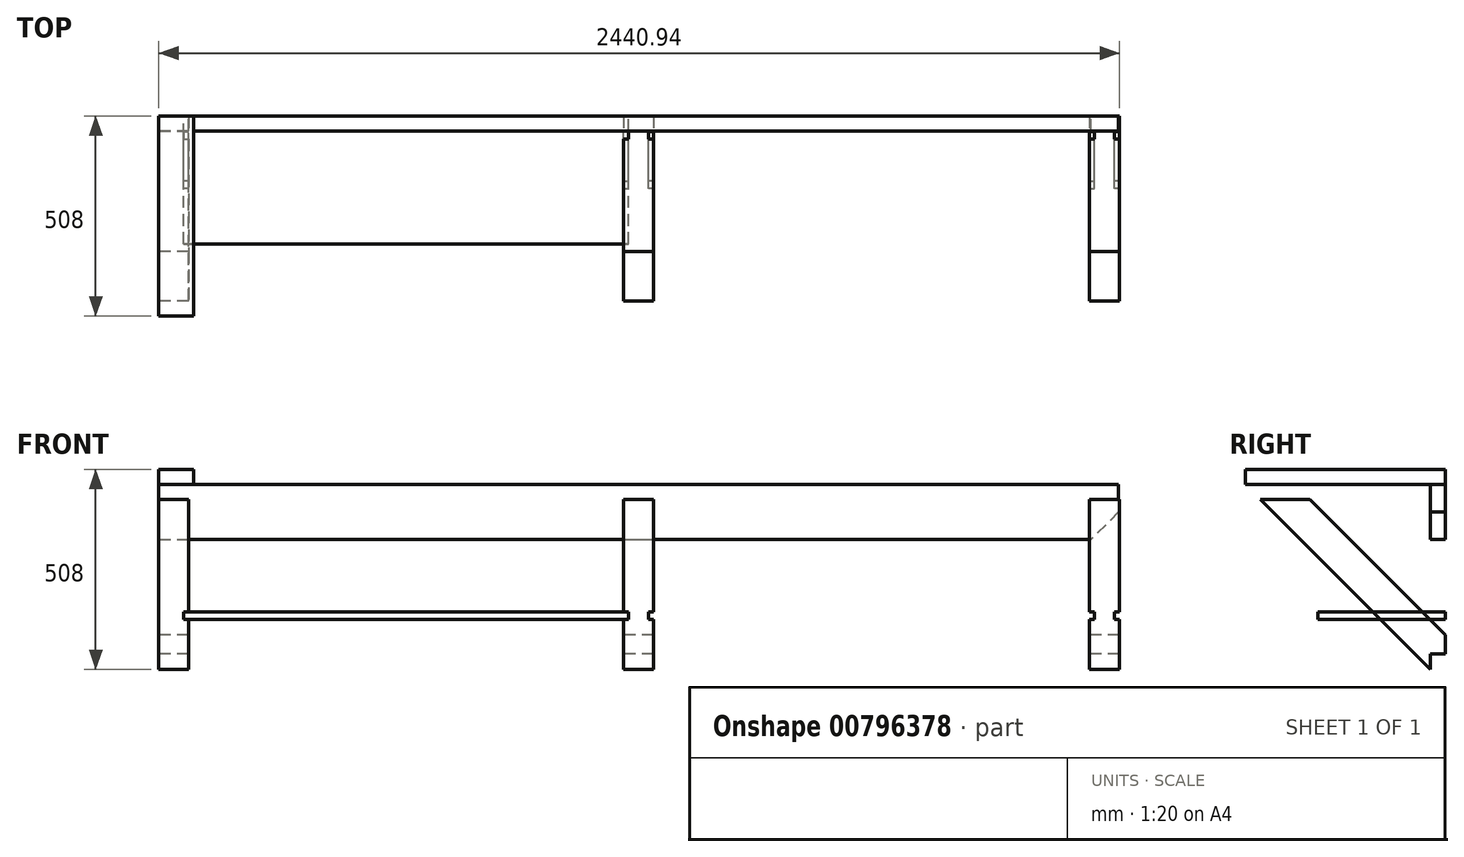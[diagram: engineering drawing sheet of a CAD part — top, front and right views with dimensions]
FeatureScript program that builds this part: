
annotation { "Feature Type Name" : "Feature", "Feature Type Description" : "" }
export const myFeature = defineFeature(function(context is Context, id is Id, definition is map)
    precondition{}
    {
        {
            var Q0;
            Q0=qCreatedBy(makeId("Front.planeOp"),FACE);
            var sketch = newSketch(context, id + "F0", { "sketchPlane" : qUnion([Q0])});
            skLineSegment(sketch, "E0.bottom", {"start": v(0, 0) * mm, "end": v(2438.4, 0) * mm});
            skLineSegment(sketch, "E0.top", {"start": v(0, -139.7) * mm, "end": v(2368.55, -139.7) * mm});
            skLineSegment(sketch, "E0.left", {"start": v(0, 0) * mm, "end": v(0, -139.7) * mm});
            skLineSegment(sketch, "E0.right", {"start": v(2438.4, 0) * mm, "end": v(2438.4, -69.85) * mm});
            skLineSegment(sketch, "E1", {"start": v(2438.4, -69.85) * mm, "end": v(2368.55, -139.7) * mm});
            skLineSegment(sketch, "E2", {"start": v(1219.2, 0) * mm, "end": v(1219.2, -139.7) * mm, "construction": true});
            skSolve(sketch);
        }
        {
            var Q0;
            Q0=makeQuery(id+"F0.imprint","IMPRINT",FACE,{"disambiguationData":[TD([[makeQuery(id+"F0.imprint","IMPRINT",EDGE,{"derivedFrom":sQuery(id+"F0.wireOp",EDGE,"E0.bottom")}),-1.0]])]});
            extrude(context, id + "F1", {"entities" : qUnion([Q0]), "depth" : 38.1 * mm, "offsetDistance" : 25.4 * mm});
        }
        {
            var Q0;
            Q0=qCreatedBy(makeId("Right.planeOp"),FACE);
            var sketch = newSketch(context, id + "F2", { "sketchPlane" : qUnion([Q0])});
            skLineSegment(sketch, "E3.bottom", {"start": v(0, 0) * mm, "end": v(-508, 0) * mm});
            skLineSegment(sketch, "E3.top", {"start": v(0, 38.1) * mm, "end": v(-508, 38.1) * mm});
            skLineSegment(sketch, "E3.left", {"start": v(0, 0) * mm, "end": v(0, 38.1) * mm});
            skLineSegment(sketch, "E3.right", {"start": v(-508, 0) * mm, "end": v(-508, 38.1) * mm});
            skLineSegment(sketch, "E4.0.0", {"start": v(0, 0) * mm, "end": v(0, -139.7) * mm});
            skLineSegment(sketch, "E4.0.1", {"start": v(0, -139.7) * mm, "end": v(-38.1, -139.7) * mm});
            skLineSegment(sketch, "E4.0.2", {"start": v(-38.1, -139.7) * mm, "end": v(-38.1, 0) * mm});
            skLineSegment(sketch, "E4.0.3", {"start": v(-38.1, 0) * mm, "end": v(0, 0) * mm});
            skLineSegment(sketch, "E5.bottom", {"start": v(-508, 0) * mm, "end": v(-38.1, 0) * mm});
            skLineSegment(sketch, "E5.top", {"start": v(-469.9, -38.1) * mm, "end": v(-38.1, -38.1) * mm});
            skLineSegment(sketch, "E5.right", {"start": v(-38.1, 0) * mm, "end": v(-38.1, -38.1) * mm});
            skLineSegment(sketch, "E6", {"start": v(-508, 0) * mm, "end": v(-469.9, -38.1) * mm});
            skSolve(sketch);
        }
        {
            var Q0;
            Q0=makeQuery(id+"F2.imprint","IMPRINT",FACE,{"disambiguationData":[TD([[makeQuery(id+"F2.imprint","IMPRINT",EDGE,{"derivedFrom":sQuery(id+"F2.wireOp",EDGE,"E3.top")}),1.0]])]});
            var Q1;
            Q1=makeQuery(id+"F2.imprint","IMPRINT",FACE,{"disambiguationData":[TD([[makeQuery(id+"F2.imprint","IMPRINT",EDGE,{"derivedFrom":sQuery(id+"F2.wireOp",EDGE,"E5.bottom")}),-1.0]])]});
            extrude(context, id + "F3", {"entities" : qUnion([Q0, Q1]), "depth" : 88.9 * mm, "offsetDistance" : 25.4 * mm});
        }
        {
            var Q0;
            Q0=qCreatedBy(makeId("Right.planeOp"),FACE);
            var sketch = newSketch(context, id + "F4", { "sketchPlane" : qUnion([Q0])});
            skLineSegment(sketch, "E7.bottom", {"start": v(0, -429.96) * mm, "end": v(-38.1, -429.96) * mm});
            skLineSegment(sketch, "E7.top", {"start": v(0, -518.86) * mm, "end": v(-38.1, -518.86) * mm});
            skLineSegment(sketch, "E7.left", {"start": v(0, -429.96) * mm, "end": v(0, -518.86) * mm});
            skLineSegment(sketch, "E7.right", {"start": v(-38.1, -429.96) * mm, "end": v(-38.1, -518.86) * mm});
            skLineSegment(sketch, "E8", {"start": v(0, 3.65) * mm, "end": v(0, -712.43) * mm, "construction": true});
            skSolve(sketch);
        }
        {
            var Q0;
            Q0=makeQuery(id+"F4.imprint","IMPRINT",FACE,{"disambiguationData":[TD([[makeQuery(id+"F4.imprint","IMPRINT",EDGE,{"derivedFrom":sQuery(id+"F4.wireOp",EDGE,"E7.bottom")}),1.0]])]});
            extrude(context, id + "F5", {"entities" : qUnion([Q0]), "depth" : 2438.4 * mm, "offsetDistance" : 25.4 * mm});
        }
        {
            var Q0;
            Q0=qCreatedBy(makeId("Right.planeOp"),FACE);
            var sketch = newSketch(context, id + "F6", { "sketchPlane" : qUnion([Q0])});
            skLineSegment(sketch, "E9", {"start": v(-469.9, -38.1) * mm, "end": v(0, -508) * mm});
            skLineSegment(sketch, "E10", {"start": v(0, -382.28) * mm, "end": v(-344.18, -38.1) * mm});
            skLineSegment(sketch, "E11", {"start": v(-344.18, -38.1) * mm, "end": v(-469.9, -38.1) * mm});
            skLineSegment(sketch, "E12", {"start": v(-230.82, -151.45) * mm, "end": v(-293.69, -214.31) * mm, "construction": true});
            skLineSegment(sketch, "E13.0.0", {"start": v(-508, 38.1) * mm, "end": v(-508, 0) * mm});
            skLineSegment(sketch, "E13.0.1", {"start": v(-508, 0) * mm, "end": v(-469.9, -38.1) * mm});
            skLineSegment(sketch, "E13.0.2", {"start": v(-469.9, -38.1) * mm, "end": v(-38.1, -38.1) * mm});
            skLineSegment(sketch, "E13.0.3", {"start": v(-38.1, -38.1) * mm, "end": v(-38.1, 0) * mm});
            skLineSegment(sketch, "E13.0.4", {"start": v(-38.1, 0) * mm, "end": v(0, 0) * mm});
            skLineSegment(sketch, "E13.0.5", {"start": v(0, 0) * mm, "end": v(0, 38.1) * mm});
            skLineSegment(sketch, "E13.0.6", {"start": v(0, 38.1) * mm, "end": v(-508, 38.1) * mm});
            skLineSegment(sketch, "E14", {"start": v(0, -382.28) * mm, "end": v(0, -508) * mm});
            skLineSegment(sketch, "E15.0", {"start": v(0, 0) * mm, "end": v(0, -139.7) * mm});
            skLineSegment(sketch, "E16", {"start": v(0, -69.85) * mm, "end": v(0, -594.76) * mm, "construction": true});
            skSolve(sketch);
        }
        {
            var Q0;
            {var subQ0=sQuery(id+"F6.wireOp",EDGE,"E9");Q0=makeQuery(id+"F6.imprint","IMPRINT",FACE,{"disambiguationData":[TD([[makeQuery(id+"F6.imprint","IMPRINT",EDGE,{"derivedFrom":subQ0}),1.0]])]});}
            extrude(context, id + "F7", {"entities" : qUnion([Q0]), "depth" : 76.2 * mm, "offsetDistance" : 25.4 * mm});
        }
        {
            var Q0;
            Q0 = qSketchRegion(id + "F4", true);
            extrude(context, id + "F8", {"entities" : qUnion([Q0]), "operationType" : NewBodyOperationType.REMOVE, "endBound" : BoundingType.THROUGH_ALL, "depth" : 25.4 * mm, "offsetDistance" : 25.4 * mm});
        }
        {
            var Q0;
            Q0=makeQuery(id+"F7.opExtrude","SWEPT_BODY",BODY,{"disambiguationData":[OSD([sQuery(id+"F6.wireOp",EDGE,"E9"),sQuery(id+"F6.wireOp",EDGE,"E10"),sQuery(id+"F6.wireOp",EDGE,"E13.0.2"),sQuery(id+"F6.wireOp",EDGE,"E14")])]});
            transform(context, id + "F9", {"entities" : qUnion([Q0]), "transformType" : TransformType.TRANSLATION_3D, "dx" : 1181.1 * mm, "dy" : 0 * mm, "dz" : 0 * mm, "makeCopy" : true});
        }
        {
            var Q0;
            Q0=qCreatedBy(makeId("Front.planeOp"),FACE);
            var sketch = newSketch(context, id + "F10", { "sketchPlane" : qUnion([Q0])});
            skLineSegment(sketch, "E17.bottom", {"start": v(1181.1, -323.85) * mm, "end": v(1193.8, -323.85) * mm});
            skLineSegment(sketch, "E17.top", {"start": v(1181.1, -342.9) * mm, "end": v(1193.8, -342.9) * mm});
            skLineSegment(sketch, "E17.left", {"start": v(1181.1, -323.85) * mm, "end": v(1181.1, -342.9) * mm});
            skLineSegment(sketch, "E17.right", {"start": v(1193.8, -323.85) * mm, "end": v(1193.8, -342.9) * mm});
            skLineSegment(sketch, "E18.bottom", {"start": v(1257.3, -323.85) * mm, "end": v(1244.6, -323.85) * mm});
            skLineSegment(sketch, "E18.top", {"start": v(1257.3, -342.9) * mm, "end": v(1244.6, -342.9) * mm});
            skLineSegment(sketch, "E18.left", {"start": v(1257.3, -323.85) * mm, "end": v(1257.3, -342.9) * mm});
            skLineSegment(sketch, "E18.right", {"start": v(1244.6, -323.85) * mm, "end": v(1244.6, -342.9) * mm});
            skLineSegment(sketch, "E19", {"start": v(1181.1, -323.85) * mm, "end": v(1257.3, -323.85) * mm, "construction": true});
            skLineSegment(sketch, "E20", {"start": v(1181.1, -342.9) * mm, "end": v(1181.1, -469.9) * mm, "construction": true});
            skSolve(sketch);
        }
        {
            var Q0;
            Q0=makeQuery(id+"F10.imprint","IMPRINT",FACE,{"disambiguationData":[TD([[makeQuery(id+"F10.imprint","IMPRINT",EDGE,{"derivedFrom":sQuery(id+"F10.wireOp",EDGE,"E17.bottom")}),-1.0]])]});
            var Q1;
            Q1=makeQuery(id+"F10.imprint","IMPRINT",FACE,{"disambiguationData":[TD([[makeQuery(id+"F10.imprint","IMPRINT",EDGE,{"derivedFrom":sQuery(id+"F10.wireOp",EDGE,"E18.bottom")}),1.0]])]});
            extrude(context, id + "F11", {"entities" : qUnion([Q0, Q1]), "operationType" : NewBodyOperationType.REMOVE, "endBound" : BoundingType.THROUGH_ALL, "depth" : 25.4 * mm, "offsetDistance" : 25.4 * mm});
        }
        {
            var Q0;
            Q0=qCreatedBy(makeId("Front.planeOp"),FACE);
            var sketch = newSketch(context, id + "F12", { "sketchPlane" : qUnion([Q0])});
            skLineSegment(sketch, "E21.0.0", {"start": v(0, -469.9) * mm, "end": v(76.2, -469.9) * mm});
            skLineSegment(sketch, "E21.0.1", {"start": v(76.2, -469.9) * mm, "end": v(76.2, -38.1) * mm});
            skLineSegment(sketch, "E21.0.2", {"start": v(76.2, -38.1) * mm, "end": v(0, -38.1) * mm});
            skLineSegment(sketch, "E21.0.3", {"start": v(0, -38.1) * mm, "end": v(0, -469.9) * mm});
            skLineSegment(sketch, "E22.bottom", {"start": v(76.2, -323.85) * mm, "end": v(63.5, -323.85) * mm});
            skLineSegment(sketch, "E22.top", {"start": v(76.2, -342.9) * mm, "end": v(63.5, -342.9) * mm});
            skLineSegment(sketch, "E22.left", {"start": v(76.2, -323.85) * mm, "end": v(76.2, -342.9) * mm});
            skLineSegment(sketch, "E22.right", {"start": v(63.5, -323.85) * mm, "end": v(63.5, -342.9) * mm});
            skLineSegment(sketch, "E23", {"start": v(76.2, -342.9) * mm, "end": v(76.2, -469.9) * mm});
            skSolve(sketch);
        }
        {
            var Q0;
            Q0=makeQuery(id+"F12.imprint","IMPRINT",FACE,{"disambiguationData":[TD([[makeQuery(id+"F12.imprint","IMPRINT",EDGE,{"derivedFrom":sQuery(id+"F12.wireOp",EDGE,"E22.bottom")}),1.0]])]});
            extrude(context, id + "F13", {"entities" : qUnion([Q0]), "operationType" : NewBodyOperationType.REMOVE, "depth" : 299.72 * mm, "offsetDistance" : 25.4 * mm});
        }
        {
            var Q0;
            Q0=qCreatedBy(makeId("Front.planeOp"),FACE);
            var sketch = newSketch(context, id + "F14", { "sketchPlane" : qUnion([Q0])});
            skLineSegment(sketch, "E24.0.0", {"start": v(1193.8, -342.9) * mm, "end": v(1181.1, -342.9) * mm});
            skLineSegment(sketch, "E24.0.1", {"start": v(1181.1, -342.9) * mm, "end": v(1181.1, -469.9) * mm});
            skLineSegment(sketch, "E24.0.2", {"start": v(1181.1, -469.9) * mm, "end": v(1257.3, -469.9) * mm});
            skLineSegment(sketch, "E24.0.3", {"start": v(1257.3, -469.9) * mm, "end": v(1257.3, -342.9) * mm});
            skLineSegment(sketch, "E24.0.4", {"start": v(1257.3, -342.9) * mm, "end": v(1244.6, -342.9) * mm});
            skLineSegment(sketch, "E24.0.5", {"start": v(1244.6, -342.9) * mm, "end": v(1244.6, -323.85) * mm});
            skLineSegment(sketch, "E24.0.6", {"start": v(1244.6, -323.85) * mm, "end": v(1257.3, -323.85) * mm});
            skLineSegment(sketch, "E24.0.7", {"start": v(1257.3, -323.85) * mm, "end": v(1257.3, -38.1) * mm});
            skLineSegment(sketch, "E24.0.8", {"start": v(1257.3, -38.1) * mm, "end": v(1181.1, -38.1) * mm});
            skLineSegment(sketch, "E24.0.9", {"start": v(1181.1, -38.1) * mm, "end": v(1181.1, -323.85) * mm});
            skLineSegment(sketch, "E24.0.10", {"start": v(1181.1, -323.85) * mm, "end": v(1193.8, -323.85) * mm});
            skLineSegment(sketch, "E24.0.11", {"start": v(1193.8, -323.85) * mm, "end": v(1193.8, -342.9) * mm});
            skLineSegment(sketch, "E25.bottom", {"start": v(1193.8, -323.85) * mm, "end": v(63.5, -323.85) * mm});
            skLineSegment(sketch, "E25.top", {"start": v(1193.8, -342.9) * mm, "end": v(63.5, -342.9) * mm});
            skLineSegment(sketch, "E25.right", {"start": v(63.5, -323.85) * mm, "end": v(63.5, -342.9) * mm});
            skSolve(sketch);
        }
        {
            var Q0;
            {var subQ3=sQuery(id+"F14.wireOp",EDGE,"E24.0.11");Q0=makeQuery(id+"F14.imprint","IMPRINT",FACE,{"disambiguationData":[TD([[makeQuery(id+"F14.imprint","IMPRINT",EDGE,{"derivedFrom":subQ3}),-1.0]])]});}
            extrude(context, id + "F15", {"entities" : qUnion([Q0]), "depth" : 324.87 * mm, "offsetDistance" : 25.4 * mm});
        }
        {
            var Q0;
            Q0=makeQuery(id+"F9.opPattern","COPY",BODY,{"derivedFrom":makeQuery(id+"F7.opExtrude","SWEPT_BODY",BODY,{"disambiguationData":[OSD([sQuery(id+"F6.wireOp",EDGE,"E9"),sQuery(id+"F6.wireOp",EDGE,"E10"),sQuery(id+"F6.wireOp",EDGE,"E13.0.2"),sQuery(id+"F6.wireOp",EDGE,"E14")])]}),"instanceName":"1"});
            transform(context, id + "F16", {"entities" : qUnion([Q0]), "transformType" : TransformType.TRANSLATION_3D, "dx" : 1183.64 * mm, "dy" : 0 * mm, "dz" : 0 * mm, "makeCopy" : true});
        }
    });
